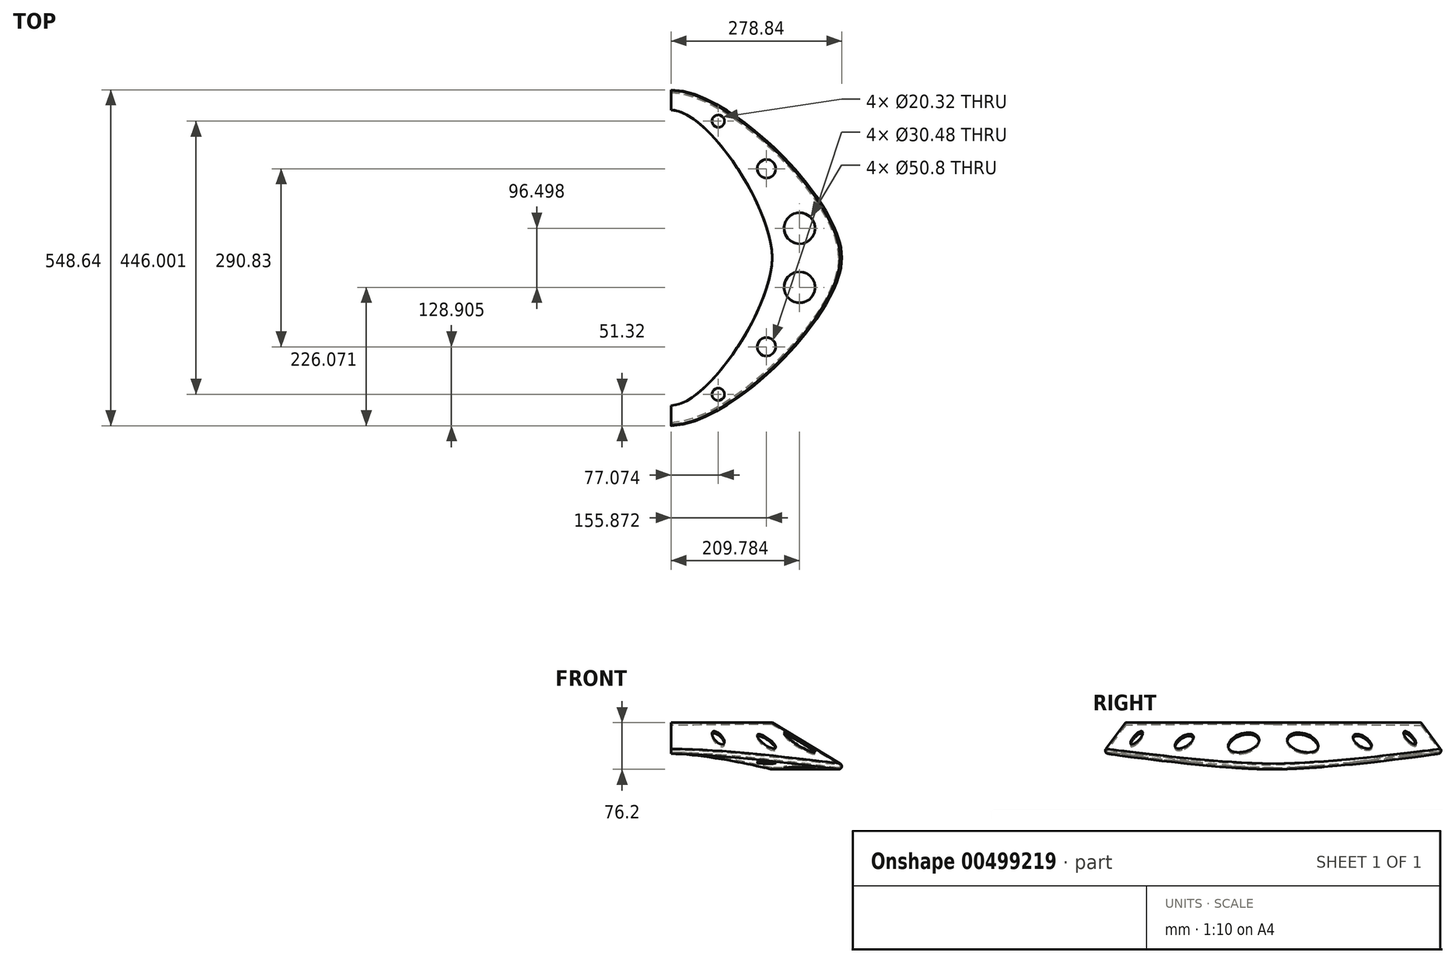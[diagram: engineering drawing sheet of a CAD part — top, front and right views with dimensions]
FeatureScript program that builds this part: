
annotation { "Feature Type Name" : "Feature", "Feature Type Description" : "" }
export const myFeature = defineFeature(function(context is Context, id is Id, definition is map)
    precondition{}
    {
        {
            var Q0;
            Q0=qCreatedBy(makeId("Top.planeOp"),FACE);
            var sketch = newSketch(context, id + "F0", { "sketchPlane" : qUnion([Q0])});
            skLineSegment(sketch, "E0", {"start": v(0, 0) * mm, "end": v(127, 0) * mm});
            skArc(sketch, "E1", {"start": v(127, 0) * mm, "mid": v(153.94, 11.16) * mm, "end": v(165.1, 38.1) * mm});
            skLineSegment(sketch, "E2", {"start": v(165.1, 38.1) * mm, "end": v(165.1, 241.3) * mm});
            skSolve(sketch);
        }
        {
            var Q0;
            Q0=sQuery(id+"F0.wireOp",EDGE,"E2");
            var Q1;
            Q1=sQuery(id+"F0.wireOp",VERTEX,"E2.end");
            cPlane(context, id + "F1", {"entities" : qUnion([Q0, Q1]), "cplaneType" : CPlaneType.LINE_POINT, "offset" : 25.4 * mm, "width" : 152.4 * mm, "height" : 152.4 * mm});
        }
        {
            var Q0;
            Q0=qCreatedBy(makeId("Right.planeOp"),FACE);
            var sketch = newSketch(context, id + "F2", { "sketchPlane" : qUnion([Q0])});
            skLineSegment(sketch, "E3", {"start": v(0, 0) * mm, "end": v(0, -50.8) * mm});
            skLineSegment(sketch, "E4", {"start": v(0, -50.8) * mm, "end": v(-38.1, -50.8) * mm});
            skLineSegment(sketch, "E5", {"start": v(-38.1, -50.8) * mm, "end": v(0, 0) * mm});
            skSolve(sketch);
        }
        {
            var Q0;
            Q0=qCreatedBy(id+"F1.planeOp",FACE);
            var sketch = newSketch(context, id + "F3", { "sketchPlane" : qUnion([Q0])});
            skLineSegment(sketch, "E6", {"start": v(-165.1, 0) * mm, "end": v(-165.1, -76.2) * mm});
            skLineSegment(sketch, "E7", {"start": v(-165.1, 0) * mm, "end": v(-292.1, -76.2) * mm});
            skLineSegment(sketch, "E8", {"start": v(-292.1, -76.2) * mm, "end": v(-165.1, -76.2) * mm});
            skSolve(sketch);
        }
        {
            var Q0;
            Q0=makeQuery(id+"F2.imprint","IMPRINT",FACE,{"disambiguationData":[TD([[makeQuery(id+"F2.imprint","IMPRINT",EDGE,{"derivedFrom":sQuery(id+"F2.wireOp",EDGE,"E3")}),-1.0]])]});
            var Q1;
            Q1=makeQuery(id+"F3.imprint","IMPRINT",FACE,{"disambiguationData":[TD([[makeQuery(id+"F3.imprint","IMPRINT",EDGE,{"derivedFrom":sQuery(id+"F3.wireOp",EDGE,"E6")}),-1.0]])]});
            var Q2;
            Q2 = qConstructionFilter(qBodyType(qCreatedBy(id + "F0" ,EDGE), BodyType.WIRE), ConstructionObject.NO);
            loft(context, id + "F4", {"startCondition" : LoftEndDerivativeType.NORMAL_TO_PROFILE, "startMagnitude" : 1, "endCondition" : LoftEndDerivativeType.NORMAL_TO_PROFILE, "endMagnitude" : 1, "sheetProfilesArray" : [{ "sheetProfileEntities" : qUnion([Q0]) }, { "sheetProfileEntities" : qUnion([Q1]) }], "guidesArray" : [{ "guideEntities" : qUnion([Q2]), "guideDerivativeType" : LoftGuideDerivativeType.DEFAULT, "guideDerivativeMagnitude" : 1 }]});
        }
        {
            var Q0;
            Q0=makeQuery(id+"F4.opLoft","SWEPT_EDGE",EDGE,{"disambiguationData":[OSD([sQuery(id+"F2.wireOp",EDGE,"E4"),sQuery(id+"F2.wireOp",EDGE,"E5"),sQuery(id+"F3.wireOp",EDGE,"E7"),sQuery(id+"F3.wireOp",EDGE,"E8")])]});
            fillet(context, id + "F5", {"entities" : qUnion([Q0]), "radius" : 5.08 * mm, "tangentPropagation" : true, "allowEdgeOverflow" : false});
        }
        {
            var Q0;
            {var subQ0=sQuery(id+"F3.wireOp",EDGE,"E6");var subQ1=sQuery(id+"F3.wireOp",EDGE,"E8");var subQ2=sQuery(id+"F3.wireOp",EDGE,"E7");var subQ3=sQuery(id+"F2.wireOp",EDGE,"E3");var subQ4=sQuery(id+"F2.wireOp",EDGE,"E4");var subQ5=sQuery(id+"F2.wireOp",EDGE,"E5");Q0=makeQuery(id+"F4.opLoft","SWEPT_FACE",FACE,{"disambiguationData":[OSD([subQ3,subQ4,subQ5,subQ0,subQ2,subQ1]),TDD([makeQuery(id+"F2.imprint","INTERSECT",VERTEX,{"derivedFrom":[subQ3,subQ5]}),makeQuery(id+"F2.imprint","INTERSECT",VERTEX,{"derivedFrom":[subQ3,subQ4]}),makeQuery(id+"F2.imprint","IMPRINT",EDGE,{"derivedFrom":subQ3}),makeQuery(id+"F3.imprint","INTERSECT",VERTEX,{"derivedFrom":[subQ0,subQ2]}),makeQuery(id+"F3.imprint","INTERSECT",VERTEX,{"derivedFrom":[subQ0,subQ1]}),makeQuery(id+"F3.imprint","IMPRINT",EDGE,{"derivedFrom":subQ0})])]});}
            var Q1;
            Q1=makeQuery(id+"F4.opLoft","CAP_FACE",FACE,{"disambiguationData":[OSD([makeQuery(id+"F3.imprint","IMPRINT",FACE,{"disambiguationData":[TD([[makeQuery(id+"F3.imprint","IMPRINT",EDGE,{"derivedFrom":sQuery(id+"F3.wireOp",EDGE,"E6")}),-1.0]])]})])],"isStart":true});
            var Q2;
            Q2=makeQuery(id+"F4.opLoft","CAP_FACE",FACE,{"disambiguationData":[OSD([makeQuery(id+"F2.imprint","IMPRINT",FACE,{"disambiguationData":[TD([[makeQuery(id+"F2.imprint","IMPRINT",EDGE,{"derivedFrom":sQuery(id+"F2.wireOp",EDGE,"E3")}),-1.0]])]})])],"isStart":true});
            shell(context, id + "F6", {"entities" : qUnion([Q0, Q1, Q2]), "thickness" : 2.54 * mm});
        }
        {
            var Q0;
            Q0=qCreatedBy(makeId("Top.planeOp"),FACE);
            var sketch = newSketch(context, id + "F7", { "sketchPlane" : qUnion([Q0])});
            skCircle(sketch, "E9", {"center": v(209.78, 193.05) * mm, "radius": 25.4 * mm});
            skCircle(sketch, "E10", {"center": v(155.87, 95.88) * mm, "radius": 15.24 * mm});
            skCircle(sketch, "E11", {"center": v(77.07, 18.3) * mm, "radius": 10.16 * mm});
            skSolve(sketch);
        }
        {
            var Q0;
            Q0=makeQuery(id+"F7.imprint","IMPRINT",FACE,{"disambiguationData":[TD([[makeQuery(id+"F7.imprint","IMPRINT",EDGE,{"derivedFrom":sQuery(id+"F7.wireOp",EDGE,"E9")}),1.0]])]});
            var Q1;
            Q1=makeQuery(id+"F7.imprint","IMPRINT",FACE,{"disambiguationData":[TD([[makeQuery(id+"F7.imprint","IMPRINT",EDGE,{"derivedFrom":sQuery(id+"F7.wireOp",EDGE,"E10")}),1.0]])]});
            var Q2;
            Q2=makeQuery(id+"F7.imprint","IMPRINT",FACE,{"disambiguationData":[TD([[makeQuery(id+"F7.imprint","IMPRINT",EDGE,{"derivedFrom":sQuery(id+"F7.wireOp",EDGE,"E11")}),1.0]])]});
            extrude(context, id + "F8", {"entities" : qUnion([Q0, Q1, Q2]), "operationType" : NewBodyOperationType.REMOVE, "endBound" : BoundingType.THROUGH_ALL, "oppositeDirection" : true, "depth" : 25.4 * mm});
        }
        {
            var Q0;
            Q0=makeQuery(id+"F4.opLoft","SWEPT_BODY",BODY,{"disambiguationData":[OSD([makeQuery(id+"F2.imprint","IMPRINT",FACE,{"disambiguationData":[TD([[makeQuery(id+"F2.imprint","IMPRINT",EDGE,{"derivedFrom":sQuery(id+"F2.wireOp",EDGE,"E3")}),-1.0]])]}),makeQuery(id+"F3.imprint","IMPRINT",FACE,{"disambiguationData":[TD([[makeQuery(id+"F3.imprint","IMPRINT",EDGE,{"derivedFrom":sQuery(id+"F3.wireOp",EDGE,"E6")}),-1.0]])]})])]});
            var Q1;
            Q1=qCreatedBy(id+"F1.planeOp",FACE);
            mirror(context, id + "F9", {"operationType" : NewBodyOperationType.ADD, "entities" : qUnion([Q0]), "mirrorPlane" : qUnion([Q1])});
        }
    });
